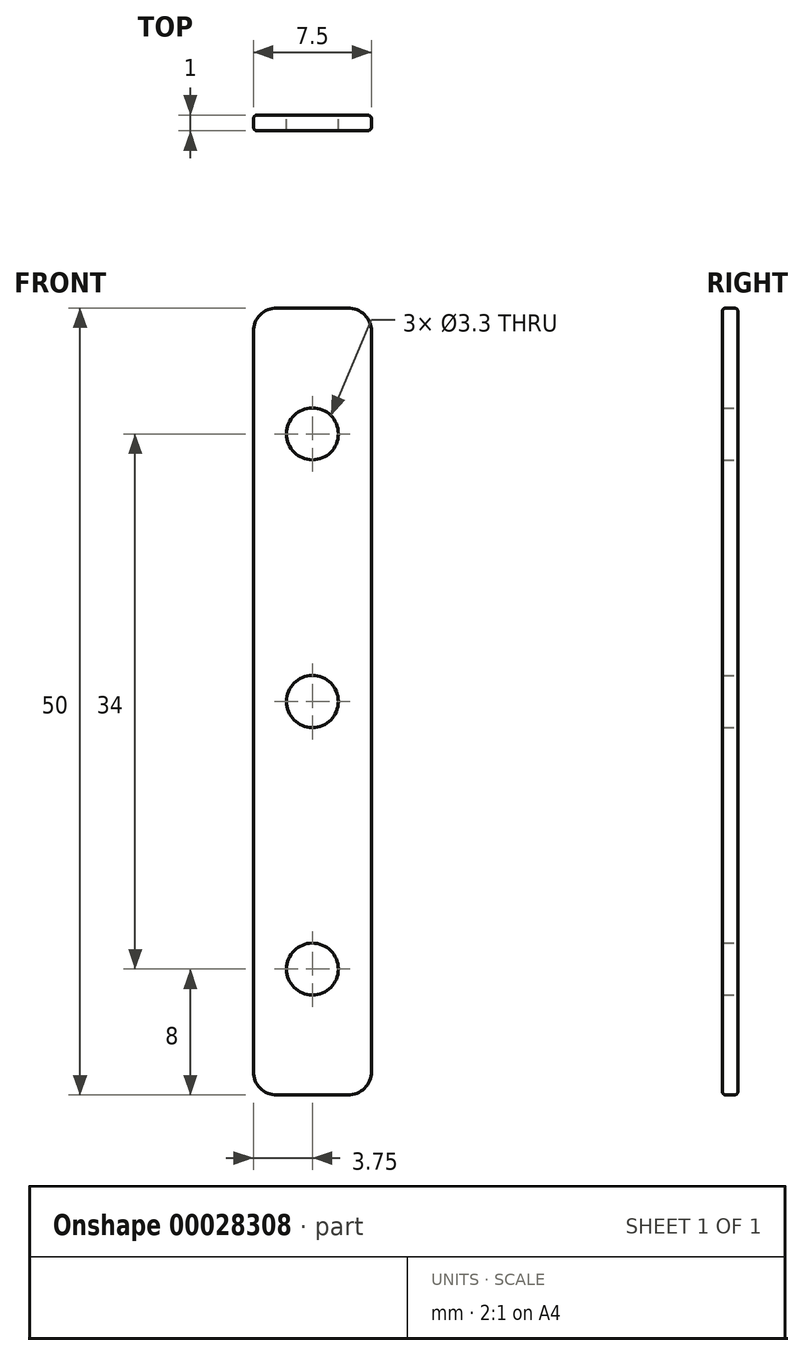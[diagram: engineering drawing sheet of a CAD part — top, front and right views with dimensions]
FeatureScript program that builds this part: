
annotation { "Feature Type Name" : "Feature", "Feature Type Description" : "" }
export const myFeature = defineFeature(function(context is Context, id is Id, definition is map)
    precondition{}
    {
        {
            var Q0;
            Q0=qCreatedBy(makeId("Front.planeOp"),FACE);
            var sketch = newSketch(context, id + "F0", { "sketchPlane" : qUnion([Q0])});
            skLineSegment(sketch, "E0.bottom", {"start": v(0, 0) * mm, "end": v(7.5, 0) * mm});
            skLineSegment(sketch, "E0.top", {"start": v(0, 50) * mm, "end": v(7.5, 50) * mm});
            skLineSegment(sketch, "E0.left", {"start": v(0, 0) * mm, "end": v(0, 50) * mm});
            skLineSegment(sketch, "E0.right", {"start": v(7.5, 0) * mm, "end": v(7.5, 50) * mm});
            skSolve(sketch);
        }
        {
            var Q0;
            Q0=makeQuery(id+"F0.imprint","IMPRINT",FACE,{"disambiguationData":[TD([[makeQuery(id+"F0.imprint","IMPRINT",EDGE,{"derivedFrom":sQuery(id+"F0.wireOp",EDGE,"E0.bottom")}),1.0]])]});
            extrude(context, id + "F1", {"entities" : qUnion([Q0]), "depth" : 1 * mm});
        }
        {
            var Q0;
            Q0=makeQuery(id+"F1.opExtrude","SWEPT_EDGE",EDGE,{"disambiguationData":[OSD([sQuery(id+"F0.wireOp",EDGE,"E0.top"),sQuery(id+"F0.wireOp",EDGE,"E0.right")])]});
            var Q1;
            Q1=makeQuery(id+"F1.opExtrude","SWEPT_EDGE",EDGE,{"disambiguationData":[OSD([sQuery(id+"F0.wireOp",EDGE,"E0.bottom"),sQuery(id+"F0.wireOp",EDGE,"E0.right")])]});
            var Q2;
            Q2=makeQuery(id+"F1.opExtrude","SWEPT_EDGE",EDGE,{"disambiguationData":[OSD([sQuery(id+"F0.wireOp",EDGE,"E0.top"),sQuery(id+"F0.wireOp",EDGE,"E0.left")])]});
            var Q3;
            Q3=makeQuery(id+"F1.opExtrude","SWEPT_EDGE",EDGE,{"disambiguationData":[OSD([sQuery(id+"F0.wireOp",EDGE,"E0.bottom"),sQuery(id+"F0.wireOp",EDGE,"E0.left")])]});
            fillet(context, id + "F2", {"entities" : qUnion([Q0, Q1, Q2, Q3]), "radius" : 1.5 * mm, "tangentPropagation" : true, "allowEdgeOverflow" : false});
        }
        {
            var Q0;
            Q0=makeQuery(id+"F1.opExtrude","CAP_FACE",FACE,{"disambiguationData":[OSD([sQuery(id+"F0.wireOp",EDGE,"E0.bottom"),sQuery(id+"F0.wireOp",EDGE,"E0.top"),sQuery(id+"F0.wireOp",EDGE,"E0.left"),sQuery(id+"F0.wireOp",EDGE,"E0.right")])],"isStart":false});
            var sketch = newSketch(context, id + "F3", { "sketchPlane" : qUnion([Q0])});
            skLineSegment(sketch, "E1.0.0", {"start": v(0, 48.5) * mm, "end": v(0, 1.5) * mm});
            skArc(sketch, "E1.0.1", {"start": v(0, 1.5) * mm, "mid": v(0.44, 0.44) * mm, "end": v(1.5, 0) * mm});
            skLineSegment(sketch, "E1.0.2", {"start": v(1.5, 0) * mm, "end": v(6, 0) * mm});
            skArc(sketch, "E1.0.3", {"start": v(6, 0) * mm, "mid": v(7.06, 0.44) * mm, "end": v(7.5, 1.5) * mm});
            skLineSegment(sketch, "E1.0.4", {"start": v(7.5, 1.5) * mm, "end": v(7.5, 48.5) * mm});
            skArc(sketch, "E1.0.5", {"start": v(7.5, 48.5) * mm, "mid": v(7.06, 49.56) * mm, "end": v(6, 50) * mm});
            skLineSegment(sketch, "E1.0.6", {"start": v(6, 50) * mm, "end": v(1.5, 50) * mm});
            skArc(sketch, "E1.0.7", {"start": v(1.5, 50) * mm, "mid": v(0.44, 49.56) * mm, "end": v(0, 48.5) * mm});
            skLineSegment(sketch, "E2", {"start": v(3.75, 50) * mm, "end": v(3.75, 0) * mm, "construction": true});
            skPoint(sketch, "E3", {"position": v(3.75, 25) * mm});
            skPoint(sketch, "E4", {"position": v(3.75, 42) * mm});
            skPoint(sketch, "E5", {"position": v(3.75, 8) * mm});
            skSolve(sketch);
        }
        {
            var Q0;
            Q0=sQuery(id+"F3.wireOp",VERTEX,"E4");
            var Q1;
            Q1=sQuery(id+"F3.wireOp",VERTEX,"E3");
            var Q2;
            Q2=sQuery(id+"F3.wireOp",VERTEX,"E5");
            var Q3;
            Q3=makeQuery(id+"F1.opExtrude","SWEPT_BODY",BODY,{"disambiguationData":[OSD([sQuery(id+"F0.wireOp",EDGE,"E0.bottom"),sQuery(id+"F0.wireOp",EDGE,"E0.top"),sQuery(id+"F0.wireOp",EDGE,"E0.left"),sQuery(id+"F0.wireOp",EDGE,"E0.right")])]});
            hole(context, id + "F4", {"style" : HoleStyle.SIMPLE, "holeDiameter" : 3.3 * mm, "endStyle" : HoleEndStyle.THROUGH, "locations" : qUnion([Q0, Q1, Q2]), "scope" : qUnion([Q3])});
        }
        {
            var Q0;
            Q0=makeQuery(id+"F1.opExtrude","CAP_EDGE",EDGE,{"disambiguationData":[OSD([sQuery(id+"F0.wireOp",EDGE,"E0.left")])],"isStart":false});
            var Q1;
            Q1=makeQuery(id+"F1.opExtrude","CAP_EDGE",EDGE,{"disambiguationData":[OSD([sQuery(id+"F0.wireOp",EDGE,"E0.left")])],"isStart":true});
            fillet(context, id + "F5", {"entities" : qUnion([Q0, Q1]), "radius" : 0.25 * mm, "tangentPropagation" : true, "allowEdgeOverflow" : false});
        }
    });
